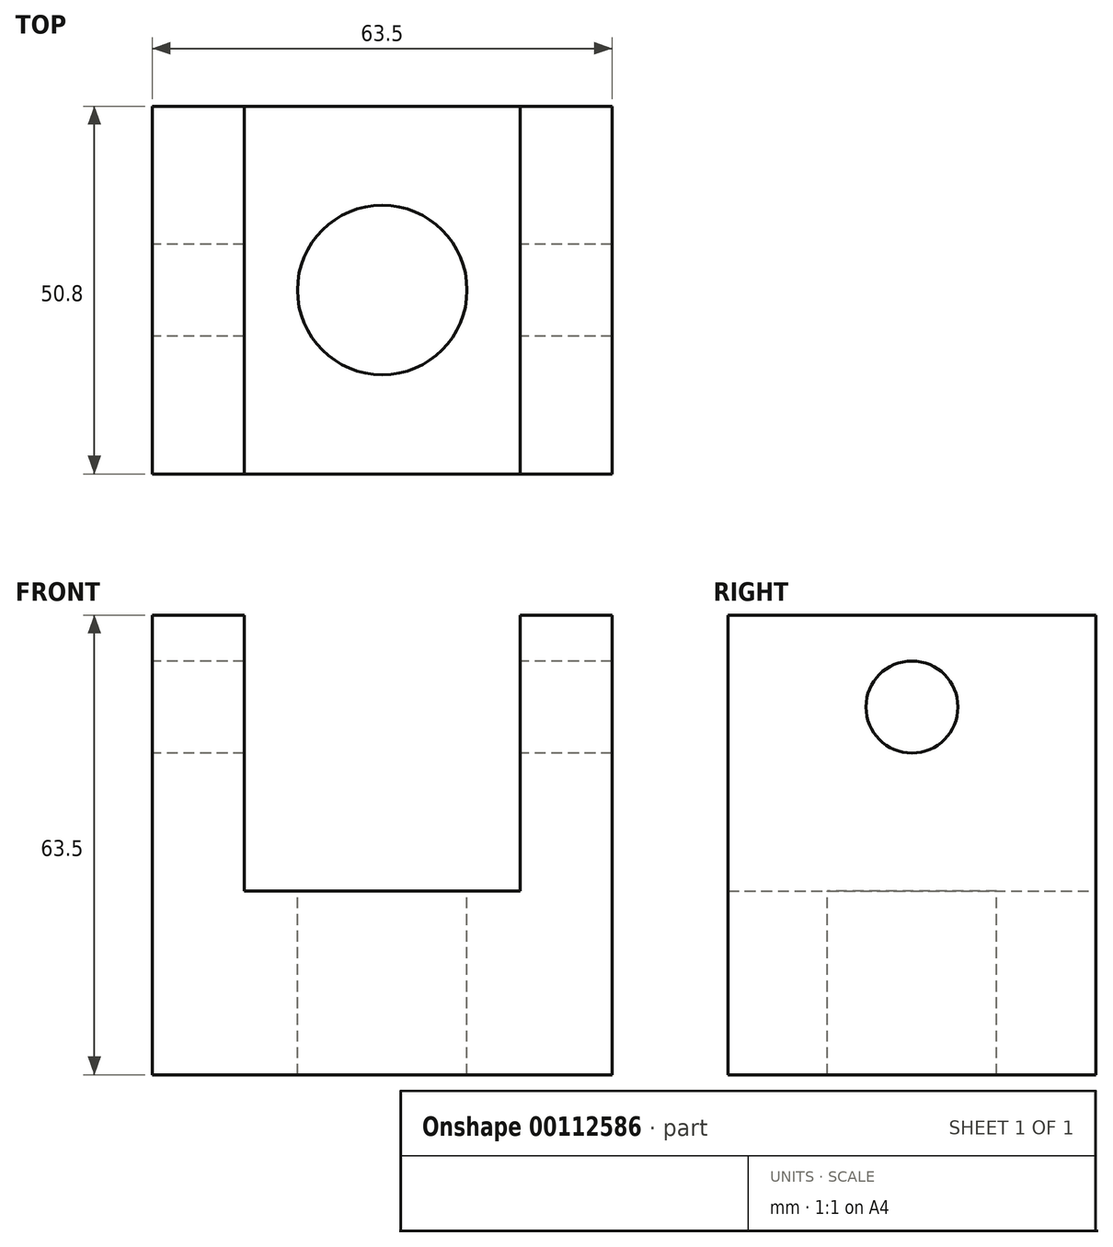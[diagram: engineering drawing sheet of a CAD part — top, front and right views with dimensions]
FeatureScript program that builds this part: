
annotation { "Feature Type Name" : "Feature", "Feature Type Description" : "" }
export const myFeature = defineFeature(function(context is Context, id is Id, definition is map)
    precondition{}
    {
        {
            var Q0;
            Q0=qCreatedBy(makeId("Front.planeOp"),FACE);
            var sketch = newSketch(context, id + "F0", { "sketchPlane" : qUnion([Q0])});
            skLineSegment(sketch, "E0.bottom", {"start": v(-31.75, 31.75) * mm, "end": v(-19.05, 31.75) * mm});
            skLineSegment(sketch, "E0.top", {"start": v(-31.75, -31.75) * mm, "end": v(31.75, -31.75) * mm});
            skLineSegment(sketch, "E0.left", {"start": v(-31.75, 31.75) * mm, "end": v(-31.75, -31.75) * mm});
            skLineSegment(sketch, "E0.right", {"start": v(31.75, 31.75) * mm, "end": v(31.75, -31.75) * mm});
            skPoint(sketch, "E0.middle", {"position": v(0, 0) * mm});
            skLineSegment(sketch, "E1.top", {"start": v(19.05, -6.35) * mm, "end": v(-19.05, -6.35) * mm});
            skLineSegment(sketch, "E1.left", {"start": v(19.05, 31.75) * mm, "end": v(19.05, -6.35) * mm});
            skLineSegment(sketch, "E1.right", {"start": v(-19.05, 31.75) * mm, "end": v(-19.05, -6.35) * mm});
            skPoint(sketch, "E1.middle", {"position": v(0, 12.7) * mm});
            skLineSegment(sketch, "E2.trimOffspring", {"start": v(19.05, 31.75) * mm, "end": v(31.75, 31.75) * mm});
            skSolve(sketch);
        }
        {
            var Q0;
            Q0 = qSketchRegion(id + "F0", true);
            extrude(context, id + "F1", {"entities" : qUnion([Q0]), "endBound" : BoundingType.SYMMETRIC, "depth" : 50.8 * mm});
        }
        {
            var Q0;
            Q0=makeQuery(id+"F1.opExtrude","SWEPT_FACE",FACE,{"disambiguationData":[OSD([sQuery(id+"F0.wireOp",EDGE,"E0.left")])]});
            var sketch = newSketch(context, id + "F2", { "sketchPlane" : qUnion([Q0])});
            skLineSegment(sketch, "E3", {"start": v(0, 19.05) * mm, "end": v(0, 31.75) * mm, "construction": true});
            skSolve(sketch);
        }
        {
            var Q0;
            Q0=sQuery(id+"F2.wireOp",VERTEX,"E3.start");
            var Q1;
            Q1=makeQuery(id+"F1.opExtrude","SWEPT_BODY",BODY,{"disambiguationData":[OSD([sQuery(id+"F0.wireOp",EDGE,"E0.bottom"),sQuery(id+"F0.wireOp",EDGE,"E0.top"),sQuery(id+"F0.wireOp",EDGE,"E0.left"),sQuery(id+"F0.wireOp",EDGE,"E0.right"),sQuery(id+"F0.wireOp",EDGE,"E1.top"),sQuery(id+"F0.wireOp",EDGE,"E1.left"),sQuery(id+"F0.wireOp",EDGE,"E1.right"),sQuery(id+"F0.wireOp",EDGE,"E2.trimOffspring")])]});
            hole(context, id + "F3", {"style" : HoleStyle.SIMPLE, "endStyle" : HoleEndStyle.THROUGH, "holeDiameter" : 12.7 * mm, "locations" : qUnion([Q0]), "scope" : qUnion([Q1]), "isTappedThrough" : true});
        }
        {
            var Q0;
            Q0=makeQuery(id+"F1.opExtrude","SWEPT_FACE",FACE,{"disambiguationData":[OSD([sQuery(id+"F0.wireOp",EDGE,"E1.top")])]});
            var sketch = newSketch(context, id + "F4", { "sketchPlane" : qUnion([Q0])});
            skLineSegment(sketch, "E4", {"start": v(0, 0) * mm, "end": v(19.05, 0) * mm, "construction": true});
            skSolve(sketch);
        }
        {
            var Q0;
            Q0=sQuery(id+"F4.wireOp",VERTEX,"E4.start");
            var Q1;
            Q1=makeQuery(id+"F1.opExtrude","SWEPT_BODY",BODY,{"disambiguationData":[OSD([sQuery(id+"F0.wireOp",EDGE,"E0.bottom"),sQuery(id+"F0.wireOp",EDGE,"E0.top"),sQuery(id+"F0.wireOp",EDGE,"E0.left"),sQuery(id+"F0.wireOp",EDGE,"E0.right"),sQuery(id+"F0.wireOp",EDGE,"E1.top"),sQuery(id+"F0.wireOp",EDGE,"E1.left"),sQuery(id+"F0.wireOp",EDGE,"E1.right"),sQuery(id+"F0.wireOp",EDGE,"E2.trimOffspring")])]});
            hole(context, id + "F5", {"style" : HoleStyle.SIMPLE, "endStyle" : HoleEndStyle.THROUGH, "standardTappedOrClearance" : lookupTablePath({ "standard" : "ANSI", "engagement" : "75%", "pitch" : "12 tpi", "size" : "1", "type" : "Tapped" }), "standardBlindInLast" : lookupTablePath({ "standard" : "ANSI", "engagement" : "75%", "pitch" : "12 tpi", "size" : "1", "type" : "Tapped" }), "holeDiameter" : 23.42 * mm, "locations" : qUnion([Q0]), "scope" : qUnion([Q1]), "isTappedThrough" : true, "majorDiameter" : 25.4 * mm, "showTappedDepth" : true});
        }
    });
